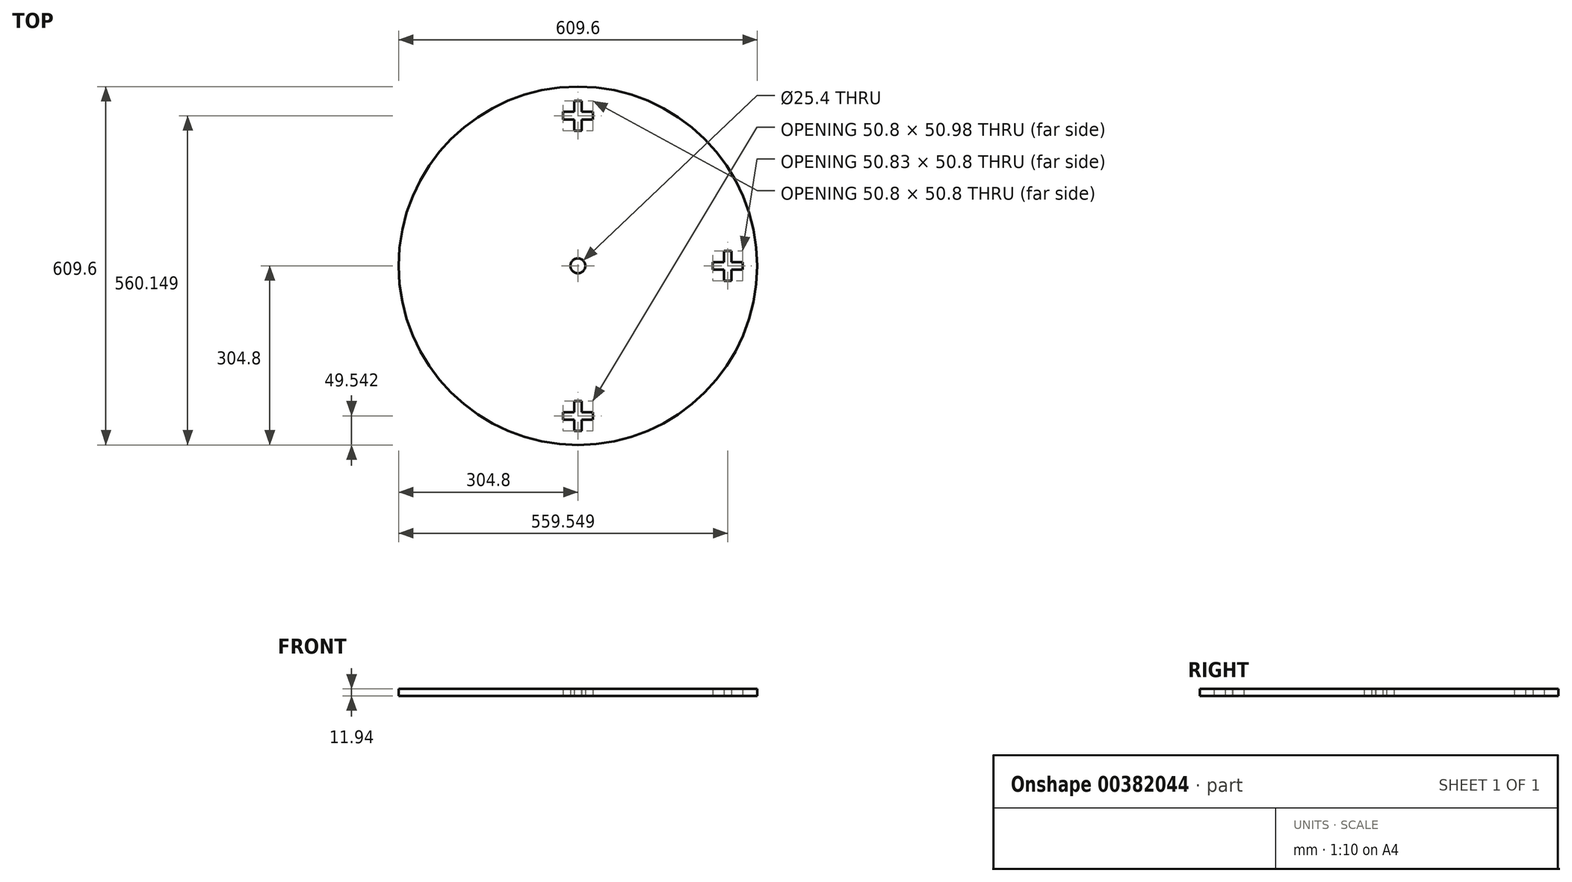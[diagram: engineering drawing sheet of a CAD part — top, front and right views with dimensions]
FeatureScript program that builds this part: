
annotation { "Feature Type Name" : "Feature", "Feature Type Description" : "" }
export const myFeature = defineFeature(function(context is Context, id is Id, definition is map)
    precondition{}
    {
        {
            var Q0;
            Q0=qCreatedBy(makeId("Top.planeOp"),FACE);
            var sketch = newSketch(context, id + "F0", { "sketchPlane" : qUnion([Q0])});
            skCircle(sketch, "E0", {"center": v(0, 0) * mm, "radius": 304.8 * mm});
            skCircle(sketch, "E1", {"center": v(0, 0) * mm, "radius": 12.7 * mm});
            skSolve(sketch);
        }
        {
            var Q0;
            Q0=makeQuery(id+"F0.imprint","IMPRINT",FACE,{"disambiguationData":[TD([[makeQuery(id+"F0.imprint","IMPRINT",EDGE,{"derivedFrom":sQuery(id+"F0.wireOp",EDGE,"E0")}),1.0]])]});
            extrude(context, id + "F1", {"entities" : qUnion([Q0]), "depth" : 11.94 * mm});
        }
        {
            var Q0;
            Q0=makeQuery(id+"F1.opExtrude","CAP_FACE",FACE,{"disambiguationData":[OSD([sQuery(id+"F0.wireOp",EDGE,"E0"),sQuery(id+"F0.wireOp",EDGE,"E1")])],"isStart":true});
            var sketch = newSketch(context, id + "F2", { "sketchPlane" : qUnion([Q0])});
            skLineSegment(sketch, "E2", {"start": v(248.78, 25.4) * mm, "end": v(260.74, 25.4) * mm});
            skLineSegment(sketch, "E3", {"start": v(280.16, 5.98) * mm, "end": v(280.16, -5.98) * mm});
            skLineSegment(sketch, "E4", {"start": v(260.74, -25.4) * mm, "end": v(248.78, -25.4) * mm});
            skLineSegment(sketch, "E5.MirrorCS", {"start": v(-5.8, 229.77) * mm, "end": v(6.16, 229.77) * mm});
            skLineSegment(sketch, "E6", {"start": v(0, 0) * mm, "end": v(0, -50.8) * mm, "construction": true});
            skLineSegment(sketch, "E7.MirrorCS", {"start": v(-229.34, 5.98) * mm, "end": v(-229.34, -5.98) * mm});
            skLineSegment(sketch, "E8", {"start": v(-248.26, 6.48) * mm, "end": v(-229.34, 6.48) * mm});
            skLineSegment(sketch, "E9", {"start": v(-248.26, -6.48) * mm, "end": v(-229.34, -6.48) * mm});
            skLineSegment(sketch, "E10", {"start": v(-229.34, -5.98) * mm, "end": v(-229.34, -6.48) * mm});
            skPoint(sketch, "E11.orphan", {"position": v(-229.34, 5.98) * mm});
            skPoint(sketch, "E12.orphan", {"position": v(-229.34, -5.98) * mm});
            skLineSegment(sketch, "E13", {"start": v(-229.34, 5.98) * mm, "end": v(-229.34, 6.48) * mm});
            skLineSegment(sketch, "E14.MirrorCS", {"start": v(-261.21, 6.48) * mm, "end": v(-280.14, 6.48) * mm});
            skLineSegment(sketch, "E15.MirrorCS", {"start": v(-280.14, 5.98) * mm, "end": v(-280.14, -5.98) * mm});
            skLineSegment(sketch, "E16.MirrorCS", {"start": v(-261.21, -6.48) * mm, "end": v(-280.14, -6.48) * mm});
            skLineSegment(sketch, "E17", {"start": v(-261.21, 6.48) * mm, "end": v(-261.21, 25.4) * mm});
            skLineSegment(sketch, "E18", {"start": v(-248.26, 6.48) * mm, "end": v(-248.26, 25.4) * mm});
            skLineSegment(sketch, "E19", {"start": v(-261.21, 25.4) * mm, "end": v(-248.26, 25.4) * mm});
            skLineSegment(sketch, "E20.MirrorCS", {"start": v(-261.21, -6.48) * mm, "end": v(-261.21, -25.4) * mm});
            skLineSegment(sketch, "E21.MirrorCS", {"start": v(-248.26, -6.48) * mm, "end": v(-248.26, -25.4) * mm});
            skLineSegment(sketch, "E22.MirrorCS", {"start": v(-261.21, -25.4) * mm, "end": v(-248.26, -25.4) * mm});
            skPoint(sketch, "E23.MirrorCS.end.orphan", {"position": v(-261.21, -6.48) * mm});
            skLineSegment(sketch, "E24.MirrorCS", {"start": v(229.34, 5.98) * mm, "end": v(229.34, 6.48) * mm});
            skLineSegment(sketch, "E25.MirrorCS", {"start": v(229.34, -5.98) * mm, "end": v(229.34, -6.48) * mm});
            skLineSegment(sketch, "E26.MirrorCS", {"start": v(229.34, 5.98) * mm, "end": v(229.34, -5.98) * mm});
            skLineSegment(sketch, "E27.MirrorCS", {"start": v(261.21, 25.4) * mm, "end": v(248.26, 25.4) * mm});
            skLineSegment(sketch, "E28.MirrorCS", {"start": v(261.21, -25.4) * mm, "end": v(248.26, -25.4) * mm});
            skPoint(sketch, "E29.MirrorP", {"position": v(229.34, -5.98) * mm});
            skLineSegment(sketch, "E30.MirrorCS", {"start": v(248.26, -6.48) * mm, "end": v(248.26, -25.4) * mm});
            skLineSegment(sketch, "E31.MirrorCS", {"start": v(261.21, -6.48) * mm, "end": v(280.14, -6.48) * mm});
            skLineSegment(sketch, "E32.MirrorCS", {"start": v(261.21, 6.48) * mm, "end": v(261.21, 25.4) * mm});
            skLineSegment(sketch, "E33.MirrorCS", {"start": v(248.26, 6.48) * mm, "end": v(248.26, 25.4) * mm});
            skPoint(sketch, "E34.MirrorP", {"position": v(261.21, -6.48) * mm});
            skLineSegment(sketch, "E35.MirrorCS", {"start": v(261.21, -6.48) * mm, "end": v(261.21, -25.4) * mm});
            skLineSegment(sketch, "E36.MirrorCS", {"start": v(248.26, 6.48) * mm, "end": v(229.34, 6.48) * mm});
            skLineSegment(sketch, "E37.MirrorCS", {"start": v(261.21, 6.48) * mm, "end": v(280.14, 6.48) * mm});
            skLineSegment(sketch, "E38.MirrorCS", {"start": v(248.26, -6.48) * mm, "end": v(229.34, -6.48) * mm});
            skPoint(sketch, "E39.MirrorP", {"position": v(229.34, 5.98) * mm});
            skLineSegment(sketch, "E40", {"start": v(-261.21, 6.48) * mm, "end": v(-248.26, -6.48) * mm, "construction": true});
            skPoint(sketch, "E41", {"position": v(-254.74, 0) * mm});
            skLineSegment(sketch, "E42", {"start": v(-254.74, 0) * mm, "end": v(0, 0) * mm, "construction": true});
            skLineSegment(sketch, "E43", {"start": v(-127.37, 0) * mm, "end": v(-127.37, -33.12) * mm, "construction": true});
            skLineSegment(sketch, "E44.MirrorCS", {"start": v(-248.75, -25.4) * mm, "end": v(-248.26, -25.4) * mm});
            skLineSegment(sketch, "E45.MirrorCS", {"start": v(-260.72, -25.4) * mm, "end": v(-248.75, -25.4) * mm});
            skLineSegment(sketch, "E46.MirrorCS", {"start": v(-260.72, -25.4) * mm, "end": v(-261.21, -25.4) * mm});
            skLineSegment(sketch, "E47.MirrorCS", {"start": v(-229.34, 6.48) * mm, "end": v(-229.34, -6.48) * mm});
            skLineSegment(sketch, "E48.MirrorCS", {"start": v(-280.14, 6.48) * mm, "end": v(-280.14, -6.48) * mm});
            skLineSegment(sketch, "E49.MirrorCS", {"start": v(-260.72, 25.4) * mm, "end": v(-248.75, 25.4) * mm});
            skPoint(sketch, "E50.MirrorP", {"position": v(-260.72, -25.4) * mm});
            skPoint(sketch, "E51.MirrorP", {"position": v(-248.26, 6.48) * mm});
            skPoint(sketch, "E52.MirrorP", {"position": v(-248.75, -25.4) * mm});
            skPoint(sketch, "E53", {"position": v(0, 255.35) * mm});
            skLineSegment(sketch, "E54", {"start": v(0, 255.35) * mm, "end": v(0, 0) * mm, "construction": true});
            skLineSegment(sketch, "E55", {"start": v(0, 127.67) * mm, "end": v(-62.56, 127.67) * mm, "construction": true});
            skLineSegment(sketch, "E56.MirrorCS", {"start": v(-6.48, 261.83) * mm, "end": v(-6.48, 280.75) * mm});
            skLineSegment(sketch, "E57.MirrorCS", {"start": v(5.98, 280.75) * mm, "end": v(-5.98, 280.75) * mm});
            skLineSegment(sketch, "E58.MirrorCS", {"start": v(6.48, 261.83) * mm, "end": v(25.4, 261.83) * mm});
            skLineSegment(sketch, "E59.MirrorCS", {"start": v(6.48, 261.83) * mm, "end": v(6.48, 280.75) * mm});
            skLineSegment(sketch, "E60.MirrorCS", {"start": v(25.4, 248.87) * mm, "end": v(25.4, 261.83) * mm});
            skLineSegment(sketch, "E61.MirrorCS", {"start": v(6.48, 248.87) * mm, "end": v(25.4, 248.87) * mm});
            skLineSegment(sketch, "E62.MirrorCS", {"start": v(6.48, 248.87) * mm, "end": v(6.48, 229.95) * mm});
            skLineSegment(sketch, "E63.MirrorCS", {"start": v(-6.48, 248.87) * mm, "end": v(-6.48, 229.95) * mm});
            skLineSegment(sketch, "E64.MirrorCS", {"start": v(-6.48, 248.87) * mm, "end": v(-25.4, 248.87) * mm});
            skLineSegment(sketch, "E65.MirrorCS", {"start": v(-25.4, 248.87) * mm, "end": v(-25.4, 261.83) * mm});
            skLineSegment(sketch, "E66.MirrorCS", {"start": v(-6.48, 261.83) * mm, "end": v(-25.4, 261.83) * mm});
            skLineSegment(sketch, "E67", {"start": v(6.48, 280.75) * mm, "end": v(5.98, 280.75) * mm});
            skLineSegment(sketch, "E68", {"start": v(-6.48, 280.75) * mm, "end": v(-5.98, 280.75) * mm});
            skLineSegment(sketch, "E69.MirrorCS", {"start": v(0, -255.35) * mm, "end": v(0, 0) * mm, "construction": true});
            skLineSegment(sketch, "E70.MirrorCS", {"start": v(0, -127.67) * mm, "end": v(-62.56, -127.67) * mm, "construction": true});
            skLineSegment(sketch, "E71.MirrorCS", {"start": v(-6.48, -248.87) * mm, "end": v(-6.48, -229.95) * mm});
            skLineSegment(sketch, "E72.MirrorCS", {"start": v(5.98, -229.95) * mm, "end": v(-5.98, -229.95) * mm});
            skLineSegment(sketch, "E73.MirrorCS", {"start": v(6.48, -261.83) * mm, "end": v(6.48, -280.75) * mm});
            skLineSegment(sketch, "E74.MirrorCS", {"start": v(-6.48, -261.83) * mm, "end": v(-6.48, -280.75) * mm});
            skLineSegment(sketch, "E75.MirrorCS", {"start": v(-6.48, -248.87) * mm, "end": v(-25.4, -248.87) * mm});
            skLineSegment(sketch, "E76.MirrorCS", {"start": v(-6.48, -261.83) * mm, "end": v(-25.4, -261.83) * mm});
            skLineSegment(sketch, "E77.MirrorCS", {"start": v(6.48, -248.87) * mm, "end": v(6.48, -229.95) * mm});
            skLineSegment(sketch, "E78.MirrorCS", {"start": v(6.48, -261.83) * mm, "end": v(25.4, -261.83) * mm});
            skLineSegment(sketch, "E79.MirrorCS", {"start": v(25.4, -261.83) * mm, "end": v(25.4, -248.87) * mm});
            skLineSegment(sketch, "E80.MirrorCS", {"start": v(6.48, -248.87) * mm, "end": v(25.4, -248.87) * mm});
            skLineSegment(sketch, "E81.MirrorCS", {"start": v(-25.4, -261.83) * mm, "end": v(-25.4, -248.87) * mm});
            skLineSegment(sketch, "E82.MirrorCS", {"start": v(5.98, -280.75) * mm, "end": v(-5.98, -280.75) * mm});
            skLineSegment(sketch, "E83", {"start": v(280.16, 5.98) * mm, "end": v(280.14, 6.48) * mm});
            skLineSegment(sketch, "E84", {"start": v(280.14, -6.48) * mm, "end": v(280.16, -5.98) * mm});
            skLineSegment(sketch, "E85", {"start": v(6.16, 229.77) * mm, "end": v(6.48, 229.77) * mm});
            skLineSegment(sketch, "E86", {"start": v(6.48, 229.95) * mm, "end": v(6.48, 229.77) * mm});
            skPoint(sketch, "E86.endSnap0", {"position": v(6.48, 229.77) * mm});
            skPoint(sketch, "E87.orphan", {"position": v(6.48, 229.52) * mm});
            skPoint(sketch, "E88.orphan", {"position": v(6.8, 229.77) * mm});
            skLineSegment(sketch, "E89", {"start": v(-5.8, 229.77) * mm, "end": v(-6.48, 229.77) * mm});
            skLineSegment(sketch, "E90", {"start": v(-6.48, 229.95) * mm, "end": v(-6.48, 229.77) * mm});
            skLineSegment(sketch, "E91", {"start": v(5.98, -280.75) * mm, "end": v(6.48, -280.75) * mm});
            skLineSegment(sketch, "E92", {"start": v(-5.98, -280.75) * mm, "end": v(-6.48, -280.75) * mm});
            skLineSegment(sketch, "E93", {"start": v(5.98, -229.95) * mm, "end": v(6.48, -229.95) * mm});
            skLineSegment(sketch, "E94", {"start": v(-5.98, -229.95) * mm, "end": v(-6.48, -229.95) * mm});
            skSolve(sketch);
        }
        {
            var Q0;
            Q0=makeQuery(id+"F2.imprint","IMPRINT",FACE,{"disambiguationData":[TD([[makeQuery(id+"F2.imprint","IMPRINT",EDGE,{"derivedFrom":sQuery(id+"F2.wireOp",EDGE,"E44.MirrorCS")}),1.0]])]});
            var Q1;
            Q1=makeQuery(id+"F2.imprint","IMPRINT",FACE,{"disambiguationData":[TD([[makeQuery(id+"F2.imprint","IMPRINT",EDGE,{"derivedFrom":sQuery(id+"F2.wireOp",EDGE,"E73.MirrorCS")}),-1.0]])]});
            var Q2;
            Q2=makeQuery(id+"F2.imprint","IMPRINT",FACE,{"disambiguationData":[TD([[makeQuery(id+"F2.imprint","IMPRINT",EDGE,{"derivedFrom":sQuery(id+"F2.wireOp",EDGE,"E3")}),-1.0]])]});
            var Q3;
            Q3=makeQuery(id+"F2.imprint","IMPRINT",FACE,{"disambiguationData":[TD([[makeQuery(id+"F2.imprint","IMPRINT",EDGE,{"derivedFrom":sQuery(id+"F2.wireOp",EDGE,"E5.MirrorCS")}),1.0]])]});
            extrude(context, id + "F3", {"entities" : qUnion([Q0, Q1, Q2, Q3]), "operationType" : NewBodyOperationType.REMOVE, "oppositeDirection" : true, "depth" : 25.4 * mm});
        }
    });
